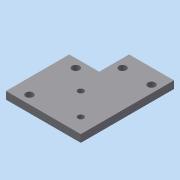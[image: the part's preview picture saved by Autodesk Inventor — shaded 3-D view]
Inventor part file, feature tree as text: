
AUTODESK INVENTOR PART (.ipt)
format: ipt  version: 2015 (Build 190159000, 159)  size: 112,640 bytes
history: native  units: mm
features: sketch x4, other x3
ambient origin geometry x8: Origin, YZ Plane, XZ Plane, XY Plane, X Axis, Y Axis, Z Axis, Center Point
bodies: Solid1 (feature_tree)
feature tree (7):
  other  "CM1.ipt"
  other  "Solid1::CM1.ipt"
  other  "TaggingFeature1"
  sketch  "Sketch1"  dims[d0=10.0mm]
  sketch  "Sketch2"
  sketch  "Sketch3"
  sketch  "Sketch4"
